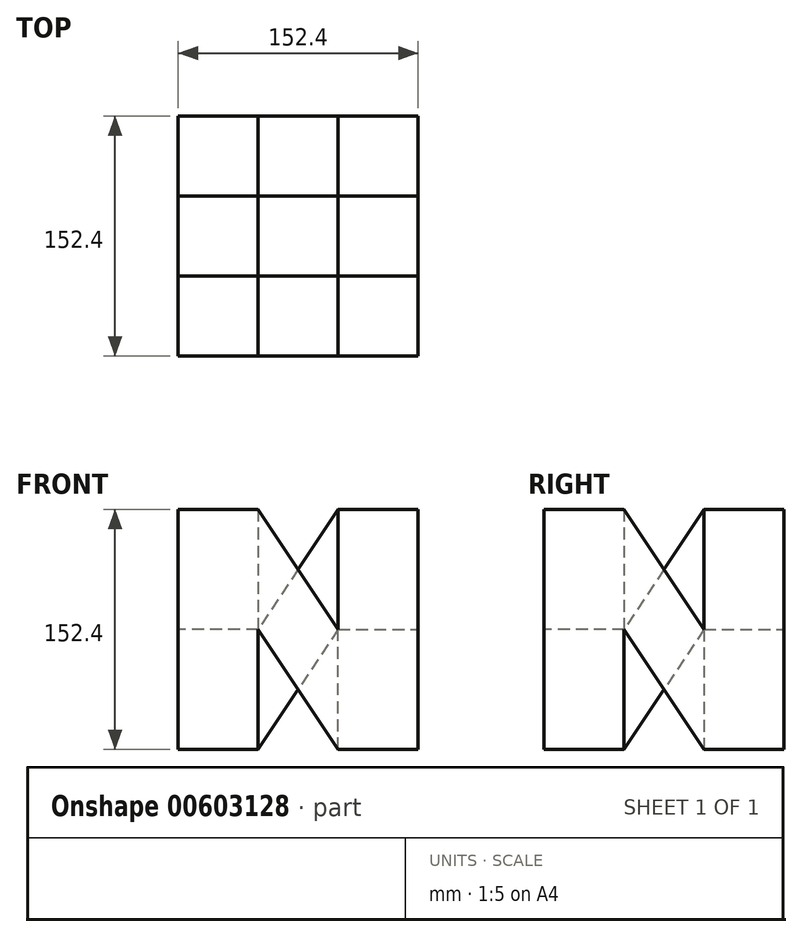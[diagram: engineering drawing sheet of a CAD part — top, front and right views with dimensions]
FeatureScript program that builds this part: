
annotation { "Feature Type Name" : "Feature", "Feature Type Description" : "" }
export const myFeature = defineFeature(function(context is Context, id is Id, definition is map)
    precondition{}
    {
        {
            var Q0;
            Q0=qCreatedBy(makeId("Top.planeOp"),FACE);
            var sketch = newSketch(context, id + "F0", { "sketchPlane" : qUnion([Q0])});
            skLineSegment(sketch, "E0.bottom", {"start": v(76.2, 80.62) * mm, "end": v(-76.2, 80.62) * mm});
            skLineSegment(sketch, "E0.top", {"start": v(76.2, -71.78) * mm, "end": v(-76.2, -71.78) * mm});
            skLineSegment(sketch, "E0.left", {"start": v(76.2, 80.62) * mm, "end": v(76.2, -71.78) * mm});
            skLineSegment(sketch, "E0.right", {"start": v(-76.2, 80.62) * mm, "end": v(-76.2, -71.78) * mm});
            skPoint(sketch, "E0.middle", {"position": v(0, 4.42) * mm});
            skSolve(sketch);
        }
        {
            var Q0;
            Q0=makeQuery(id+"F0.imprint","IMPRINT",FACE,{"disambiguationData":[TD([[makeQuery(id+"F0.imprint","IMPRINT",EDGE,{"derivedFrom":sQuery(id+"F0.wireOp",EDGE,"E0.bottom")}),1.0]])]});
            extrude(context, id + "F1", {"entities" : qUnion([Q0]), "depth" : 152.4 * mm, "offsetDistance" : 25.4 * mm, "symmetric" : true});
        }
        {
            var Q0;
            Q0=makeQuery(id+"F1.opExtrude","CAP_FACE",FACE,{"disambiguationData":[OSD([sQuery(id+"F0.wireOp",EDGE,"E0.bottom"),sQuery(id+"F0.wireOp",EDGE,"E0.top"),sQuery(id+"F0.wireOp",EDGE,"E0.left"),sQuery(id+"F0.wireOp",EDGE,"E0.right")])],"isStart":false});
            var sketch = newSketch(context, id + "F2", { "sketchPlane" : qUnion([Q0]), "disableImprinting" : false});
            skLineSegment(sketch, "E1", {"start": v(-76.2, 80.62) * mm, "end": v(-25.4, 80.62) * mm});
            skLineSegment(sketch, "E2", {"start": v(-25.4, 80.62) * mm, "end": v(25.4, 80.62) * mm});
            skLineSegment(sketch, "E3", {"start": v(-76.2, 80.62) * mm, "end": v(76.2, -71.78) * mm});
            skLineSegment(sketch, "E4", {"start": v(-76.2, 4.42) * mm, "end": v(76.2, 4.42) * mm});
            skLineSegment(sketch, "E5", {"start": v(0, 80.62) * mm, "end": v(0, -71.78) * mm});
            skLineSegment(sketch, "E6.MirrorCS", {"start": v(-76.2, 80.62) * mm, "end": v(-76.2, 29.82) * mm});
            skLineSegment(sketch, "E7.MirrorCS", {"start": v(-76.2, 29.82) * mm, "end": v(-76.2, -20.98) * mm});
            skLineSegment(sketch, "E8.MirrorCS", {"start": v(76.2, 80.62) * mm, "end": v(76.2, 29.82) * mm});
            skLineSegment(sketch, "E9.MirrorCS", {"start": v(76.2, 29.82) * mm, "end": v(76.2, -20.98) * mm});
            skLineSegment(sketch, "E10.MirrorCS", {"start": v(-76.2, -71.78) * mm, "end": v(-25.4, -71.78) * mm});
            skLineSegment(sketch, "E11.MirrorCS", {"start": v(-25.4, -71.78) * mm, "end": v(25.4, -71.78) * mm});
            skLineSegment(sketch, "E12", {"start": v(-25.4, -71.78) * mm, "end": v(-25.4, 80.62) * mm});
            skLineSegment(sketch, "E13", {"start": v(25.4, 80.62) * mm, "end": v(25.4, -71.78) * mm});
            skLineSegment(sketch, "E14", {"start": v(-76.2, 29.82) * mm, "end": v(76.2, 29.82) * mm});
            skLineSegment(sketch, "E15", {"start": v(-76.2, -20.98) * mm, "end": v(76.2, -20.98) * mm});
            skSolve(sketch);
        }
        {
            var Q0;
            {var subQ0=sQuery(id+"F2.wireOp",EDGE,"E14");var subQ3=sQuery(id+"F2.wireOp",EDGE,"E5");var subQ5=makeQuery(id+"F2.imprint","INTERSECT",VERTEX,{"derivedFrom":[subQ3,subQ0]});Q0=makeQuery(id+"F2.imprint","IMPRINT",FACE,{"disambiguationData":[TD([[makeQuery(id+"F2.imprint","IMPRINT",EDGE,{"disambiguationData":[TD([[subQ5,-1.0]])],"derivedFrom":subQ3}),-1.0]])]});}
            var Q1;
            {var subQ0=sQuery(id+"F2.wireOp",EDGE,"E13");var subQ1=sQuery(id+"F2.wireOp",EDGE,"E4");var subQ2=makeQuery(id+"F2.imprint","INTERSECT",VERTEX,{"derivedFrom":[subQ1,subQ0]});Q1=makeQuery(id+"F2.imprint","IMPRINT",FACE,{"disambiguationData":[TD([[makeQuery(id+"F2.imprint","IMPRINT",EDGE,{"disambiguationData":[TD([[subQ2,1.0]])],"derivedFrom":subQ0}),-1.0]])]});}
            var Q2;
            {var subQ0=sQuery(id+"F2.wireOp",EDGE,"E4");var subQ3=sQuery(id+"F2.wireOp",EDGE,"E13");var subQ5=makeQuery(id+"F2.imprint","INTERSECT",VERTEX,{"derivedFrom":[subQ0,subQ3]});Q2=makeQuery(id+"F2.imprint","IMPRINT",FACE,{"disambiguationData":[TD([[makeQuery(id+"F2.imprint","IMPRINT",EDGE,{"disambiguationData":[TD([[subQ5,1.0]])],"derivedFrom":subQ0}),-1.0]])]});}
            var Q3;
            {var subQ0=sQuery(id+"F2.wireOp",EDGE,"E5");var subQ3=sQuery(id+"F2.wireOp",EDGE,"E15");var subQ5=makeQuery(id+"F2.imprint","INTERSECT",VERTEX,{"derivedFrom":[subQ0,subQ3]});Q3=makeQuery(id+"F2.imprint","IMPRINT",FACE,{"disambiguationData":[TD([[makeQuery(id+"F2.imprint","IMPRINT",EDGE,{"disambiguationData":[TD([[subQ5,1.0]])],"derivedFrom":subQ0}),1.0]])]});}
            var Q4;
            {var subQ0=sQuery(id+"F2.wireOp",EDGE,"E12");var subQ1=sQuery(id+"F2.wireOp",EDGE,"E4");var subQ2=makeQuery(id+"F2.imprint","INTERSECT",VERTEX,{"derivedFrom":[subQ1,subQ0]});Q4=makeQuery(id+"F2.imprint","IMPRINT",FACE,{"disambiguationData":[TD([[makeQuery(id+"F2.imprint","IMPRINT",EDGE,{"disambiguationData":[TD([[subQ2,1.0]])],"derivedFrom":subQ0}),-1.0]])]});}
            var Q5;
            {var subQ0=sQuery(id+"F2.wireOp",EDGE,"E12");var subQ3=sQuery(id+"F2.wireOp",EDGE,"E4");var subQ5=makeQuery(id+"F2.imprint","INTERSECT",VERTEX,{"derivedFrom":[subQ3,subQ0]});Q5=makeQuery(id+"F2.imprint","IMPRINT",FACE,{"disambiguationData":[TD([[makeQuery(id+"F2.imprint","IMPRINT",EDGE,{"disambiguationData":[TD([[subQ5,-1.0]])],"derivedFrom":subQ3}),1.0]])]});}
            extrude(context, id + "F3", {"entities" : qUnion([Q0, Q1, Q2, Q3, Q4, Q5]), "operationType" : NewBodyOperationType.REMOVE, "endBound" : BoundingType.THROUGH_ALL, "oppositeDirection" : true, "depth" : 25.4 * mm, "offsetDistance" : 25.4 * mm});
        }
        {
            var Q0;
            Q0=makeQuery(id+"F1.opExtrude","SWEPT_FACE",FACE,{"disambiguationData":[OSD([sQuery(id+"F0.wireOp",EDGE,"E0.bottom")])]});
            var sketch = newSketch(context, id + "F4", { "sketchPlane" : qUnion([Q0]), "disableImprinting" : false});
            skLineSegment(sketch, "E16", {"start": v(-76.2, 76.2) * mm, "end": v(-25.4, 76.2) * mm});
            skLineSegment(sketch, "E17", {"start": v(-25.4, 76.2) * mm, "end": v(25.4, 76.2) * mm});
            skLineSegment(sketch, "E18", {"start": v(-76.2, 0) * mm, "end": v(76.2, 0) * mm});
            skLineSegment(sketch, "E19.MirrorCS", {"start": v(-76.2, -76.2) * mm, "end": v(-25.4, -76.2) * mm});
            skLineSegment(sketch, "E20.MirrorCS", {"start": v(-25.4, -76.2) * mm, "end": v(25.4, -76.2) * mm});
            skLineSegment(sketch, "E21", {"start": v(25.4, 76.2) * mm, "end": v(25.4, 0) * mm});
            skLineSegment(sketch, "E22", {"start": v(-25.4, 76.2) * mm, "end": v(25.4, 0) * mm});
            skLineSegment(sketch, "E23", {"start": v(-25.4, -76.2) * mm, "end": v(-25.4, 0) * mm});
            skLineSegment(sketch, "E24", {"start": v(-25.4, 0) * mm, "end": v(25.4, -76.2) * mm});
            skSolve(sketch);
        }
        {
            var Q0;
            Q0=makeQuery(id+"F4.imprint","IMPRINT",FACE,{"disambiguationData":[TD([[makeQuery(id+"F4.imprint","IMPRINT",EDGE,{"derivedFrom":sQuery(id+"F4.wireOp",EDGE,"E20.MirrorCS")}),1.0]])]});
            var Q1;
            Q1=makeQuery(id+"F4.imprint","IMPRINT",FACE,{"disambiguationData":[TD([[makeQuery(id+"F4.imprint","IMPRINT",EDGE,{"derivedFrom":sQuery(id+"F4.wireOp",EDGE,"E17")}),-1.0]])]});
            extrude(context, id + "F5", {"entities" : qUnion([Q0, Q1]), "operationType" : NewBodyOperationType.REMOVE, "oppositeDirection" : true, "depth" : 50.8 * mm, "offsetDistance" : 25.4 * mm});
        }
        {
            var Q0;
            Q0=makeQuery(id+"F1.opExtrude","SWEPT_FACE",FACE,{"disambiguationData":[OSD([sQuery(id+"F0.wireOp",EDGE,"E0.right")])]});
            var sketch = newSketch(context, id + "F6", { "sketchPlane" : qUnion([Q0])});
            skLineSegment(sketch, "E25", {"start": v(-80.62, 76.2) * mm, "end": v(-29.82, 76.2) * mm});
            skLineSegment(sketch, "E26", {"start": v(-29.82, 76.2) * mm, "end": v(20.98, 76.2) * mm});
            skLineSegment(sketch, "E27", {"start": v(-80.62, 0) * mm, "end": v(71.78, 0) * mm});
            skLineSegment(sketch, "E28.MirrorCS", {"start": v(-80.62, -76.2) * mm, "end": v(-29.82, -76.2) * mm});
            skLineSegment(sketch, "E29.MirrorCS", {"start": v(-29.82, -76.2) * mm, "end": v(20.98, -76.2) * mm});
            skLineSegment(sketch, "E30", {"start": v(20.98, 76.2) * mm, "end": v(20.98, 0) * mm});
            skLineSegment(sketch, "E31", {"start": v(-29.82, -76.2) * mm, "end": v(-29.82, 0) * mm});
            skLineSegment(sketch, "E32", {"start": v(-29.82, 0) * mm, "end": v(20.98, -76.2) * mm});
            skLineSegment(sketch, "E33", {"start": v(-29.82, 76.2) * mm, "end": v(20.98, 0) * mm});
            skSolve(sketch);
        }
        {
            var Q0;
            Q0=makeQuery(id+"F6.imprint","IMPRINT",FACE,{"disambiguationData":[TD([[makeQuery(id+"F6.imprint","IMPRINT",EDGE,{"derivedFrom":sQuery(id+"F6.wireOp",EDGE,"E29.MirrorCS")}),1.0]])]});
            var Q1;
            Q1=makeQuery(id+"F6.imprint","IMPRINT",FACE,{"disambiguationData":[TD([[makeQuery(id+"F6.imprint","IMPRINT",EDGE,{"derivedFrom":sQuery(id+"F6.wireOp",EDGE,"E26")}),-1.0]])]});
            extrude(context, id + "F7", {"entities" : qUnion([Q0, Q1]), "operationType" : NewBodyOperationType.REMOVE, "oppositeDirection" : true, "depth" : 50.8 * mm, "offsetDistance" : 25.4 * mm});
        }
        {
            var Q0;
            Q0=makeQuery(id+"F1.opExtrude","SWEPT_FACE",FACE,{"disambiguationData":[OSD([sQuery(id+"F0.wireOp",EDGE,"E0.top")])]});
            var sketch = newSketch(context, id + "F8", { "sketchPlane" : qUnion([Q0])});
            skLineSegment(sketch, "E34", {"start": v(-76.2, 76.2) * mm, "end": v(-25.4, 76.2) * mm});
            skLineSegment(sketch, "E35", {"start": v(-25.4, 76.2) * mm, "end": v(25.4, 76.2) * mm});
            skLineSegment(sketch, "E36", {"start": v(-76.2, 0) * mm, "end": v(76.2, 0) * mm});
            skLineSegment(sketch, "E37.MirrorCS", {"start": v(-76.2, -76.2) * mm, "end": v(-25.4, -76.2) * mm});
            skLineSegment(sketch, "E38.MirrorCS", {"start": v(-25.4, -76.2) * mm, "end": v(25.4, -76.2) * mm});
            skLineSegment(sketch, "E39", {"start": v(25.4, 76.2) * mm, "end": v(25.4, 0) * mm});
            skLineSegment(sketch, "E40", {"start": v(-25.4, 76.2) * mm, "end": v(25.4, 0) * mm});
            skLineSegment(sketch, "E41", {"start": v(-25.4, -76.2) * mm, "end": v(-25.4, 0) * mm});
            skLineSegment(sketch, "E42", {"start": v(-25.4, 0) * mm, "end": v(25.4, -76.2) * mm});
            skSolve(sketch);
        }
        {
            var Q0;
            Q0=makeQuery(id+"F8.imprint","IMPRINT",FACE,{"disambiguationData":[TD([[makeQuery(id+"F8.imprint","IMPRINT",EDGE,{"derivedFrom":sQuery(id+"F8.wireOp",EDGE,"E38.MirrorCS")}),-1.0]])]});
            var Q1;
            Q1=makeQuery(id+"F8.imprint","IMPRINT",FACE,{"disambiguationData":[TD([[makeQuery(id+"F8.imprint","IMPRINT",EDGE,{"derivedFrom":sQuery(id+"F8.wireOp",EDGE,"E35")}),1.0]])]});
            extrude(context, id + "F9", {"entities" : qUnion([Q0, Q1]), "operationType" : NewBodyOperationType.REMOVE, "oppositeDirection" : true, "depth" : 50.8 * mm, "offsetDistance" : 25.4 * mm});
        }
        {
            var Q0;
            Q0=makeQuery(id+"F1.opExtrude","SWEPT_FACE",FACE,{"disambiguationData":[OSD([sQuery(id+"F0.wireOp",EDGE,"E0.left")])]});
            var sketch = newSketch(context, id + "F10", { "sketchPlane" : qUnion([Q0])});
            skLineSegment(sketch, "E43", {"start": v(-71.78, 76.2) * mm, "end": v(-20.98, 76.2) * mm});
            skLineSegment(sketch, "E44", {"start": v(-20.98, 76.2) * mm, "end": v(29.82, 76.2) * mm});
            skLineSegment(sketch, "E45", {"start": v(-71.78, 0) * mm, "end": v(80.62, 0) * mm});
            skLineSegment(sketch, "E46.MirrorCS", {"start": v(-71.78, -76.2) * mm, "end": v(-20.98, -76.2) * mm});
            skLineSegment(sketch, "E47.MirrorCS", {"start": v(-20.98, -76.2) * mm, "end": v(29.82, -76.2) * mm});
            skLineSegment(sketch, "E48", {"start": v(29.82, 76.2) * mm, "end": v(29.82, 0) * mm});
            skLineSegment(sketch, "E49", {"start": v(-20.98, -76.2) * mm, "end": v(-20.98, 0) * mm});
            skLineSegment(sketch, "E50", {"start": v(-20.98, 0) * mm, "end": v(29.82, -76.2) * mm});
            skLineSegment(sketch, "E51", {"start": v(-20.98, 76.2) * mm, "end": v(29.82, 0) * mm});
            skSolve(sketch);
        }
        {
            var Q0;
            Q0=makeQuery(id+"F10.imprint","IMPRINT",FACE,{"disambiguationData":[TD([[makeQuery(id+"F10.imprint","IMPRINT",EDGE,{"derivedFrom":sQuery(id+"F10.wireOp",EDGE,"E47.MirrorCS")}),-1.0]])]});
            var Q1;
            Q1=makeQuery(id+"F10.imprint","IMPRINT",FACE,{"disambiguationData":[TD([[makeQuery(id+"F10.imprint","IMPRINT",EDGE,{"derivedFrom":sQuery(id+"F10.wireOp",EDGE,"E44")}),1.0]])]});
            extrude(context, id + "F11", {"entities" : qUnion([Q0, Q1]), "operationType" : NewBodyOperationType.REMOVE, "oppositeDirection" : true, "depth" : 50.8 * mm, "offsetDistance" : 25.4 * mm});
        }
    });
